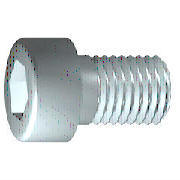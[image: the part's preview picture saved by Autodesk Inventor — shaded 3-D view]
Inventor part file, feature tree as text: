
AUTODESK INVENTOR PART (.ipt)
format: ipt  version: 2013 (Build 170138000, 138)  size: 185,344 bytes
history: native  units: mm (DEFAULTED — no unit token found)
features: sketch x2, extrude x1, plane x1, fillet x1
ambient origin geometry x7: Origin, YZ Plane, XY Plane, X Axis, Y Axis, Z Axis, Center Point
bodies: Solid1 (feature_tree), Body (feature_tree)
feature tree (5):
  extrude  "Slot"  Depth=0.24548mm
  plane  "Work Plane1"
  fillet  "Fillet2"  Radius=2.0mm
  sketch  "Sketch1"  dims[d1=8.95462mm d2=0.24548mm d3=2.0mm]
  sketch  "Sketch2"  dims[d4=1.0mm d5=60.0deg d6=2.0mm d7=2.0mm d8=1.732051mm d9=3.8mm d10=90.0deg d11=10.0mm d12=0.0mm d13=8.95462mm d14=0.0mm d15=0.24538mm d16=0.24538mm d17=0.2mm d19=0.0mm d26=10.0mm d27=45.0deg d28=0.0mm d29=0.0mm d30=0.1mm]
